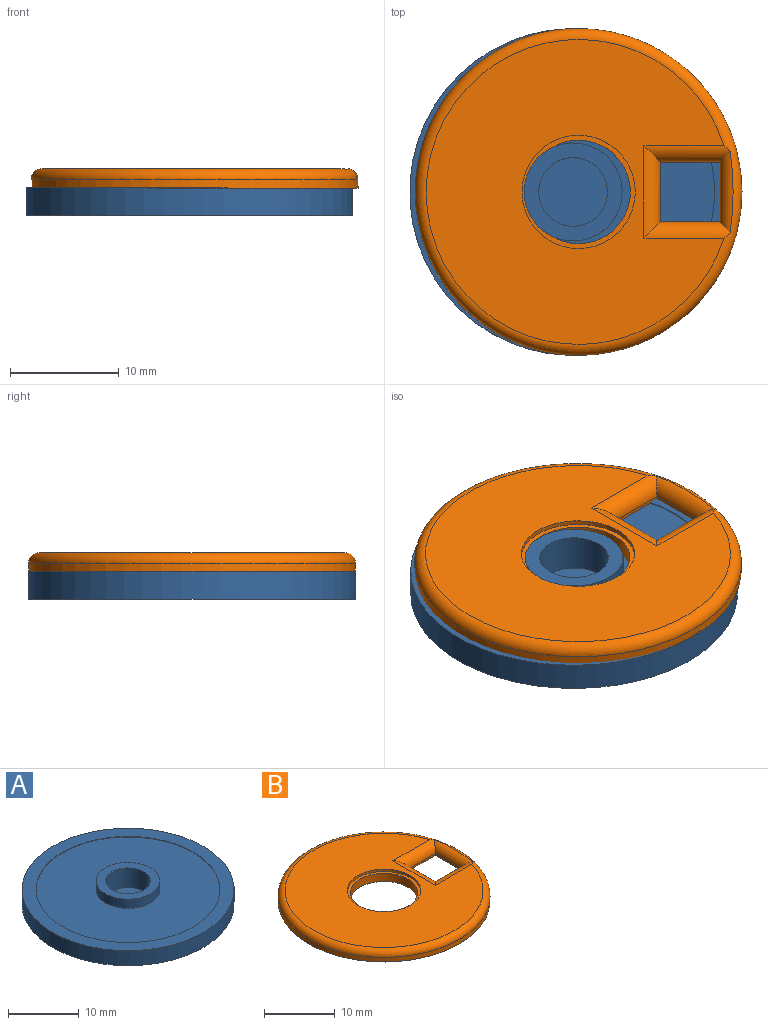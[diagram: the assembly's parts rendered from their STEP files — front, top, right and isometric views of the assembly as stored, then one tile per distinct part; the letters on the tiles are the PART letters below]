
ASSEMBLY  parts=2 mates=1
PART A: 9 faces, bbox 30x30x4.1 mm
  f0: cylinder r=13mm len=26mm, axis (0,0,-1), area 8.2mm2, adj f2,f4
  f1: cylinder r=15mm len=30mm, axis (0,0,-1), area 245mm2, adj f2,f3
  f2: plane 30x30mm, normal (0,0,1), area 175.9mm2, adj f0,f1
  f3: plane 30x30mm, normal (0,0,-1), area 706.9mm2, adj f1
  f4: plane 26x26mm, normal (0,0,1), area 467.3mm2, adj f0,f5
  f5: cylinder r=4.5mm len=9mm, axis (0,0,-1), area 45.2mm2, adj f4,f6
  f6: plane 9x9mm, normal (0,0,1), area 32.4mm2, adj f5,f7
  f7: cylinder r=3.15mm len=6.3mm, axis (0,0,1), area 67.3mm2, adj f6,f8
  f8: plane 6.3x6.3mm, normal (0,0,1), area 31.2mm2, adj f7
PART B: 15 faces, bbox 32.5x32.5x1.8 mm
  f0: cylinder r=4.75mm len=9.5mm, axis (0,0,-1), area 41.8mm2, adj f2,f14
  f1: plane 28x27.34mm, normal (0,0,1), area 464.7mm2, adj f4,f9,f10,f12,f13
  f2: plane 30x30mm, normal (0,0,-1), area 605.7mm2, adj f0,f3,f5,f6,f7,f8
  f3: cylinder r=15mm len=30mm, axis (0,0,-1), area 75.4mm2, adj f2,f4
  f4: torus R=14mm, axis (0,0,1), area 142.2mm2, adj f1,f3,f9,f10,f11
  f5: plane 5.51x0.4mm, normal (-1,0,0), area 2.2mm2, adj f2,f6,f8,f9,f10,f11
  f6: plane 5.5x0.3mm, normal (0,-1,0), area 1.6mm2, adj f2,f5,f7,f10
  f7: plane 5.5x0.3mm, normal (1,0,0), area 1.7mm2, adj f2,f6,f8,f12
  f8: plane 5.5x0.3mm, normal (0,1,0), area 1.6mm2, adj f2,f5,f7,f9
  f9: cylinder r=1.5mm len=7.91mm, axis (-1,0,0), area 15.1mm2, adj f1,f4,f5,f8,f11,f12
  f10: cylinder r=1.5mm len=7.91mm, axis (1,0,0), area 15.1mm2, adj f1,f4,f5,f6,f11,f12
  f11: cylinder r=1.4mm len=7.49mm, axis (0,-1,0), area 12mm2, adj f4,f5,f9,f10
  f12: cylinder r=1.5mm len=8.5mm, axis (0,1,0), area 15.5mm2, adj f1,f7,f9,f10
  f13: cylinder r=5.2mm len=10.4mm, axis (0,0,1), area 13.1mm2, adj f1,f14
  f14: plane 10.4x10.4mm, normal (0,0,1), area 14.1mm2, adj f0,f13
PLACE A t=(0.77,-2.46,1.41)mm
PLACE B t=(1.47,49.53,3.91)mm
MATE fastened B.f2 <-> A.f0  axis (0,0,-1) through (-16.22,8.35,3.91)mm
